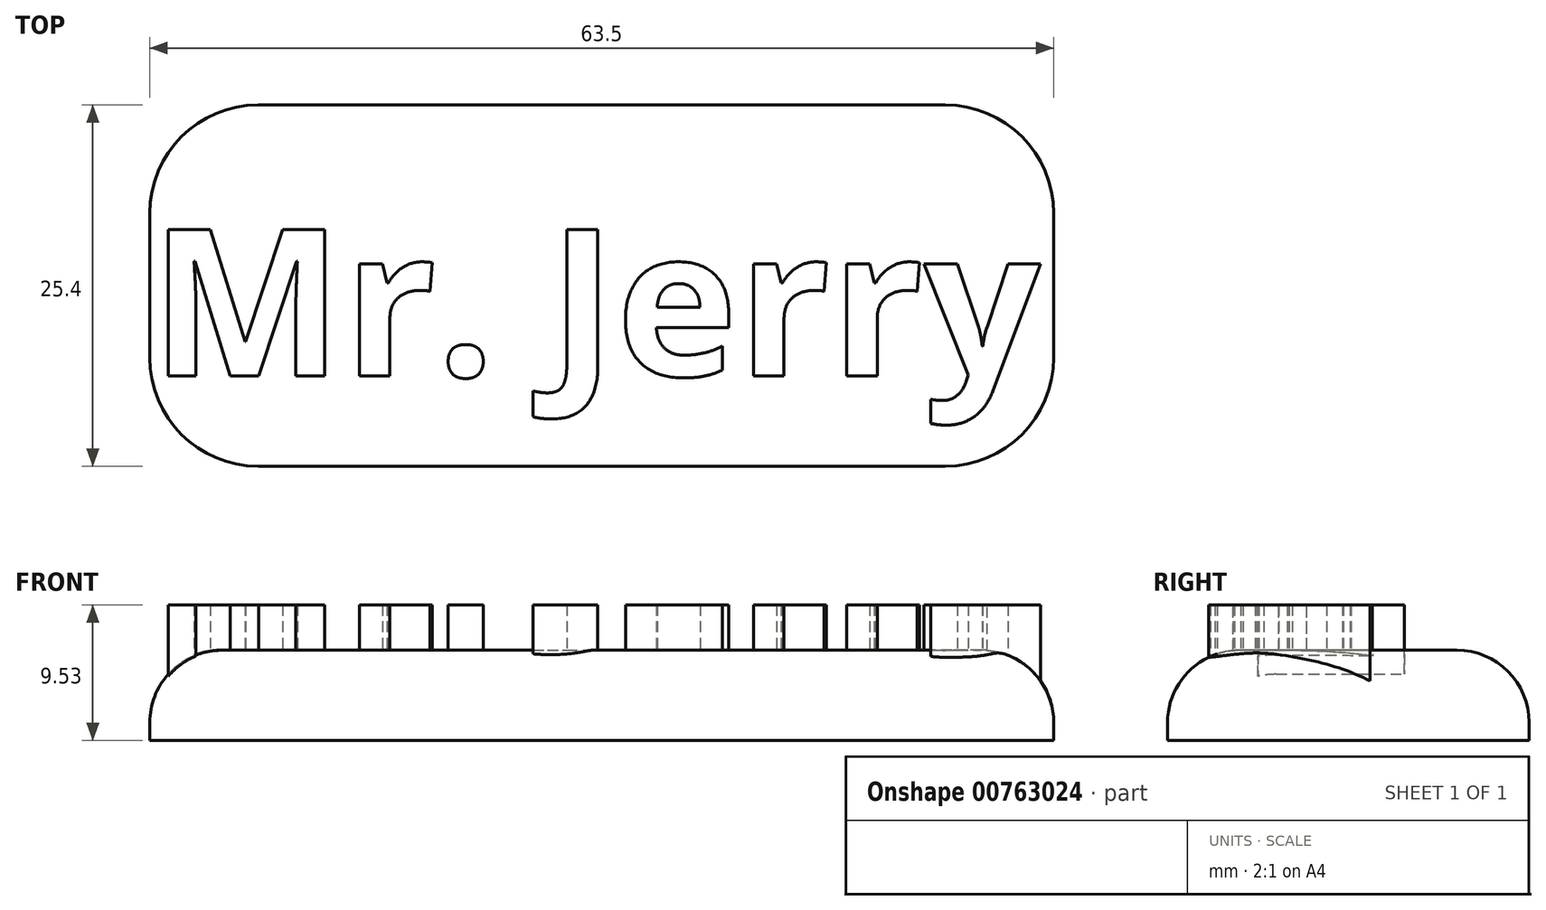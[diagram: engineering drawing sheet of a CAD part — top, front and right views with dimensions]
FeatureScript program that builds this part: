
annotation { "Feature Type Name" : "Feature", "Feature Type Description" : "" }
export const myFeature = defineFeature(function(context is Context, id is Id, definition is map)
    precondition{}
    {
        {
            var Q0;
            Q0=qCreatedBy(makeId("Top.planeOp"),FACE);
            var sketch = newSketch(context, id + "F0", { "sketchPlane" : qUnion([Q0])});
            skLineSegment(sketch, "E0.bottom", {"start": v(0, 0) * mm, "end": v(63.5, 0) * mm});
            skLineSegment(sketch, "E0.top", {"start": v(0, 25.4) * mm, "end": v(63.5, 25.4) * mm});
            skLineSegment(sketch, "E0.left", {"start": v(0, 0) * mm, "end": v(0, 25.4) * mm});
            skLineSegment(sketch, "E0.right", {"start": v(63.5, 0) * mm, "end": v(63.5, 25.4) * mm});
            skSolve(sketch);
        }
        {
            var Q0;
            Q0=makeQuery(id+"F0.imprint","IMPRINT",FACE,{"disambiguationData":[TD([[makeQuery(id+"F0.imprint","IMPRINT",EDGE,{"derivedFrom":sQuery(id+"F0.wireOp",EDGE,"E0.bottom")}),1.0]])]});
            extrude(context, id + "F1", {"entities" : qUnion([Q0]), "depth" : 6.35 * mm, "offsetDistance" : 25.4 * mm});
        }
        {
            var Q0;
            Q0=makeQuery(id+"F1.opExtrude","CAP_FACE",FACE,{"disambiguationData":[OSD([sQuery(id+"F0.wireOp",EDGE,"E0.bottom"),sQuery(id+"F0.wireOp",EDGE,"E0.top"),sQuery(id+"F0.wireOp",EDGE,"E0.left"),sQuery(id+"F0.wireOp",EDGE,"E0.right")])],"isStart":false});
            var sketch = newSketch(context, id + "F2", { "sketchPlane" : qUnion([Q0])});
            skText(sketch, "E1", { "text": "Mr. Jerry", "fontName": "OpenSans-Bold.ttf"});
            const initialGuessF2  = {"E1": [0, 0.00635, 1, 0, 0.01038]};
            skSetInitialGuess(sketch, initialGuessF2);
            skSolve(sketch);
        }
        {
            var Q0;
            Q0=makeQuery(id+"F2.imprint","IMPRINT",FACE,{"disambiguationData":[TD([[makeQuery(id+"F2.imprint","IMPRINT",EDGE,{"derivedFrom":sQuery(id+"F2.wireOp",EDGE,"E1.sketch_text.stroke-0")}),-1.0]])]});
            var Q1;
            Q1=makeQuery(id+"F2.imprint","IMPRINT",FACE,{"disambiguationData":[TD([[makeQuery(id+"F2.imprint","IMPRINT",EDGE,{"derivedFrom":sQuery(id+"F2.wireOp",EDGE,"E1.sketch_text.stroke-19")}),-1.0]])]});
            var Q2;
            Q2=makeQuery(id+"F2.imprint","IMPRINT",FACE,{"disambiguationData":[TD([[makeQuery(id+"F2.imprint","IMPRINT",EDGE,{"derivedFrom":sQuery(id+"F2.wireOp",EDGE,"E1.sketch_text.stroke-32")}),-1.0]])]});
            var Q3;
            Q3=makeQuery(id+"F2.imprint","IMPRINT",FACE,{"disambiguationData":[TD([[makeQuery(id+"F2.imprint","IMPRINT",EDGE,{"derivedFrom":sQuery(id+"F2.wireOp",EDGE,"E1.sketch_text.stroke-40")}),-1.0]])]});
            var Q4;
            Q4=makeQuery(id+"F2.imprint","IMPRINT",FACE,{"disambiguationData":[TD([[makeQuery(id+"F2.imprint","IMPRINT",EDGE,{"derivedFrom":sQuery(id+"F2.wireOp",EDGE,"E1.sketch_text.stroke-50")}),-1.0]])]});
            var Q5;
            Q5=makeQuery(id+"F2.imprint","IMPRINT",FACE,{"disambiguationData":[TD([[makeQuery(id+"F2.imprint","IMPRINT",EDGE,{"derivedFrom":sQuery(id+"F2.wireOp",EDGE,"E1.sketch_text.stroke-70")}),-1.0]])]});
            var Q6;
            Q6=makeQuery(id+"F2.imprint","IMPRINT",FACE,{"disambiguationData":[TD([[makeQuery(id+"F2.imprint","IMPRINT",EDGE,{"derivedFrom":sQuery(id+"F2.wireOp",EDGE,"E1.sketch_text.stroke-83")}),-1.0]])]});
            var Q7;
            Q7=makeQuery(id+"F2.imprint","IMPRINT",FACE,{"disambiguationData":[TD([[makeQuery(id+"F2.imprint","IMPRINT",EDGE,{"derivedFrom":sQuery(id+"F2.wireOp",EDGE,"E1.sketch_text.stroke-96")}),-1.0]])]});
            extrude(context, id + "F3", {"entities" : qUnion([Q0, Q1, Q2, Q3, Q4, Q5, Q6, Q7]), "operationType" : NewBodyOperationType.ADD, "depth" : 3.17 * mm, "offsetDistance" : 25.4 * mm});
        }
        {
            var Q0;
            Q0=makeQuery(id+"F1.opExtrude","SWEPT_EDGE",EDGE,{"disambiguationData":[OSD([sQuery(id+"F0.wireOp",EDGE,"E0.top"),sQuery(id+"F0.wireOp",EDGE,"E0.right")])]});
            var Q1;
            Q1=makeQuery(id+"F1.opExtrude","SWEPT_EDGE",EDGE,{"disambiguationData":[OSD([sQuery(id+"F0.wireOp",EDGE,"E0.top"),sQuery(id+"F0.wireOp",EDGE,"E0.left")])]});
            var Q2;
            Q2=makeQuery(id+"F1.opExtrude","SWEPT_EDGE",EDGE,{"disambiguationData":[OSD([sQuery(id+"F0.wireOp",EDGE,"E0.bottom"),sQuery(id+"F0.wireOp",EDGE,"E0.right")])]});
            var Q3;
            Q3=makeQuery(id+"F1.opExtrude","SWEPT_EDGE",EDGE,{"disambiguationData":[OSD([sQuery(id+"F0.wireOp",EDGE,"E0.bottom"),sQuery(id+"F0.wireOp",EDGE,"E0.left")])]});
            fillet(context, id + "F4", {"entities" : qUnion([Q0, Q1, Q2, Q3]), "radius" : 7.62 * mm, "tangentPropagation" : true, "allowEdgeOverflow" : false});
        }
        {
            var Q0;
            Q0=makeQuery(id+"F1.opExtrude","CAP_EDGE",EDGE,{"disambiguationData":[OSD([sQuery(id+"F0.wireOp",EDGE,"E0.bottom")])],"isStart":false});
            fillet(context, id + "F5", {"entities" : qUnion([Q0]), "radius" : 5.08 * mm, "tangentPropagation" : true, "allowEdgeOverflow" : false});
        }
    });
